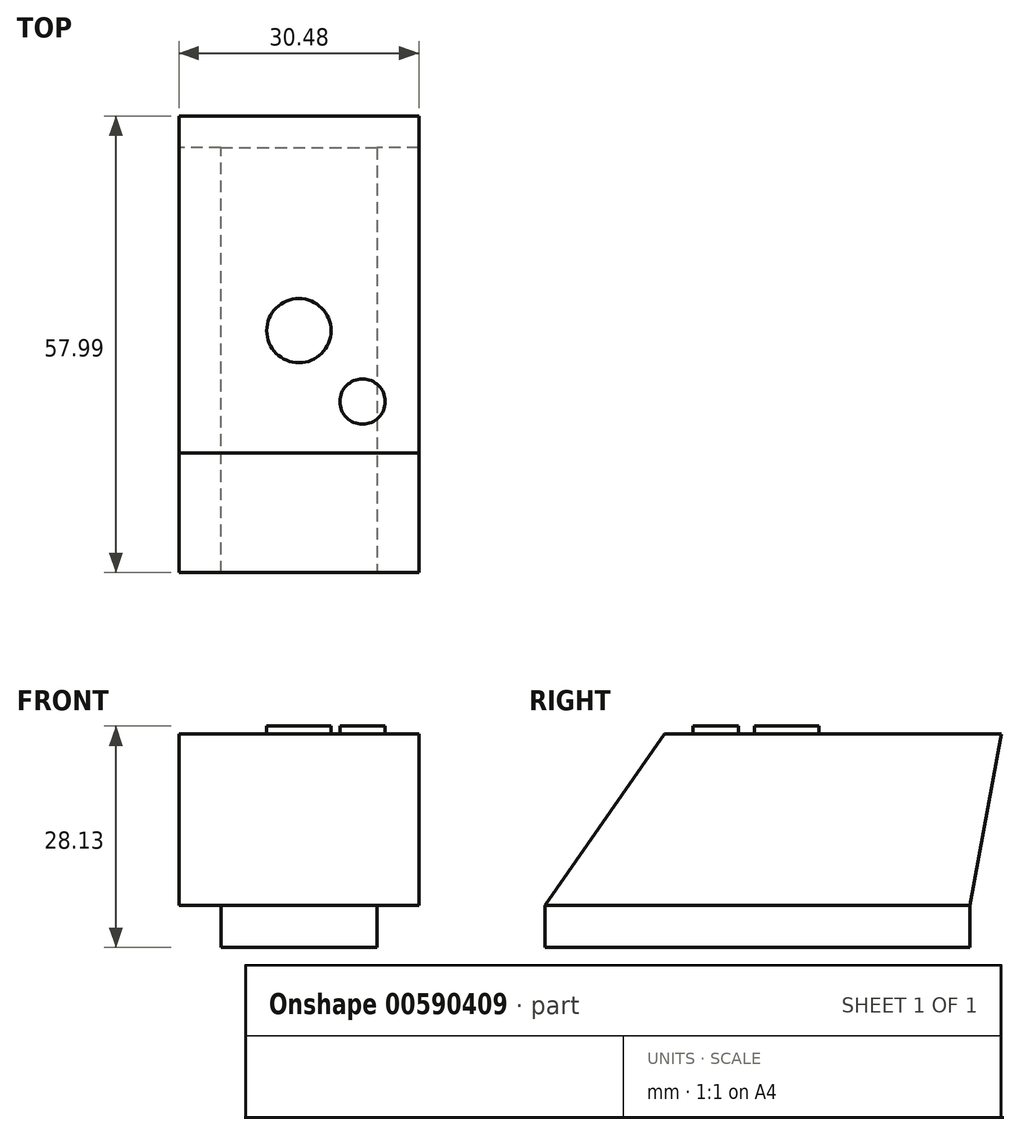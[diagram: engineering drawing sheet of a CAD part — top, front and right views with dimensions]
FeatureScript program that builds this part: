
annotation { "Feature Type Name" : "Feature", "Feature Type Description" : "" }
export const myFeature = defineFeature(function(context is Context, id is Id, definition is map)
    precondition{}
    {
        {
            var Q0;
            Q0=qCreatedBy(makeId("Right.planeOp"),FACE);
            var sketch = newSketch(context, id + "F0", { "sketchPlane" : qUnion([Q0])});
            skLineSegment(sketch, "E0", {"start": v(0, 0) * mm, "end": v(-53.98, 0) * mm});
            skLineSegment(sketch, "E1", {"start": v(-53.98, 0) * mm, "end": v(-38.8, 21.78) * mm});
            skLineSegment(sketch, "E2", {"start": v(-38.8, 21.78) * mm, "end": v(4.01, 21.78) * mm});
            skLineSegment(sketch, "E3", {"start": v(4.01, 21.78) * mm, "end": v(0, 0) * mm});
            skSolve(sketch);
        }
        {
            var Q0;
            Q0=makeQuery(id+"F0.imprint","IMPRINT",FACE,{"disambiguationData":[TD([[makeQuery(id+"F0.imprint","IMPRINT",EDGE,{"derivedFrom":sQuery(id+"F0.wireOp",EDGE,"E0")}),-1.0]])]});
            extrude(context, id + "F1", {"entities" : qUnion([Q0]), "depth" : 30.48 * mm, "offsetDistance" : 25.4 * mm});
        }
        {
            var Q0;
            Q0=makeQuery(id+"F1.opExtrude","SWEPT_FACE",FACE,{"disambiguationData":[OSD([sQuery(id+"F0.wireOp",EDGE,"E2")])]});
            var sketch = newSketch(context, id + "F2", { "sketchPlane" : qUnion([Q0])});
            skCircle(sketch, "E4", {"center": v(15.24, -23.25) * mm, "radius": 4.08 * mm});
            skPoint(sketch, "E4.centerSnap0", {"position": v(15.24, -38.8) * mm});
            skCircle(sketch, "E5", {"center": v(23.33, -32.26) * mm, "radius": 2.88 * mm});
            skSolve(sketch);
        }
        {
            var Q0;
            Q0=makeQuery(id+"F2.imprint","IMPRINT",FACE,{"disambiguationData":[TD([[makeQuery(id+"F2.imprint","IMPRINT",EDGE,{"derivedFrom":sQuery(id+"F2.wireOp",EDGE,"E4")}),1.0]])]});
            var Q1;
            Q1=makeQuery(id+"F2.imprint","IMPRINT",FACE,{"disambiguationData":[TD([[makeQuery(id+"F2.imprint","IMPRINT",EDGE,{"derivedFrom":sQuery(id+"F2.wireOp",EDGE,"E5")}),1.0]])]});
            var Q2;
            Q2=sQuery(id+"F2.wireOp",EDGE,"E4");
            extrude(context, id + "F3", {"entities" : qUnion([Q0, Q1]), "operationType" : NewBodyOperationType.ADD, "surfaceEntities" : qUnion([Q2]), "depth" : 1.02 * mm, "offsetDistance" : 25.4 * mm});
        }
        {
            var Q0;
            Q0=qCreatedBy(makeId("Top.planeOp"),FACE);
            var sketch = newSketch(context, id + "F4", { "sketchPlane" : qUnion([Q0])});
            skLineSegment(sketch, "E6", {"start": v(5.33, 0) * mm, "end": v(25.15, 0) * mm});
            skLineSegment(sketch, "E7", {"start": v(25.15, 0) * mm, "end": v(25.15, -53.98) * mm});
            skLineSegment(sketch, "E8", {"start": v(25.15, -53.98) * mm, "end": v(5.33, -53.98) * mm});
            skLineSegment(sketch, "E9", {"start": v(5.33, -53.98) * mm, "end": v(5.33, 0) * mm});
            skSolve(sketch);
        }
        {
            var Q0;
            Q0=makeQuery(id+"F4.imprint","IMPRINT",FACE,{"disambiguationData":[TD([[makeQuery(id+"F4.imprint","IMPRINT",EDGE,{"derivedFrom":sQuery(id+"F4.wireOp",EDGE,"E6")}),-1.0]])]});
            extrude(context, id + "F5", {"entities" : qUnion([Q0]), "operationType" : NewBodyOperationType.ADD, "oppositeDirection" : true, "depth" : 5.33 * mm, "offsetDistance" : 25.4 * mm});
        }
    });
